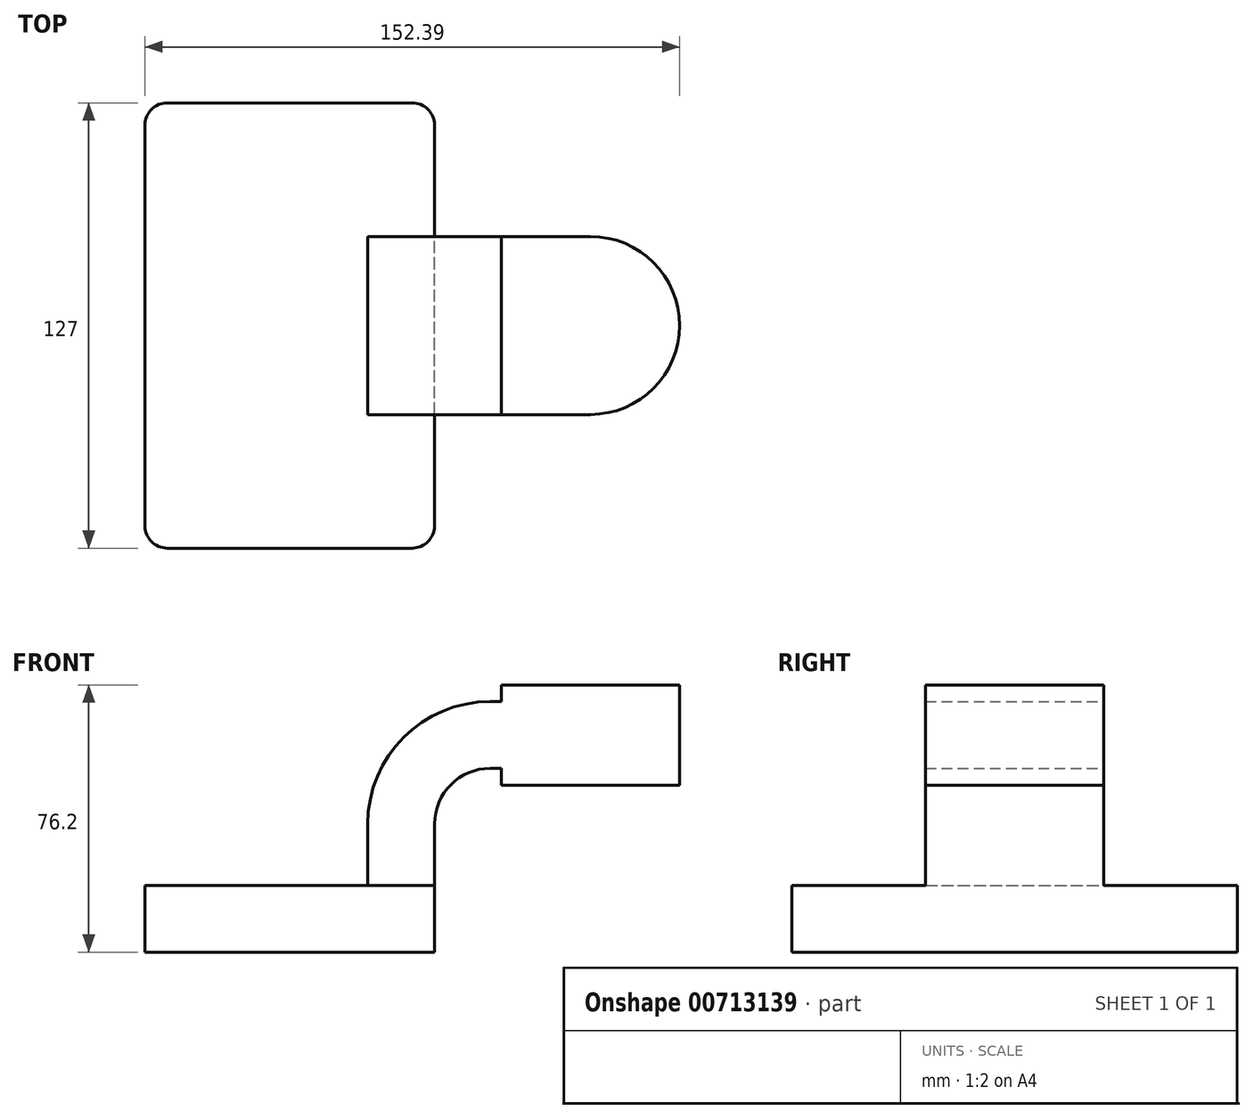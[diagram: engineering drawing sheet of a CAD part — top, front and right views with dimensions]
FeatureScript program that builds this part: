
annotation { "Feature Type Name" : "Feature", "Feature Type Description" : "" }
export const myFeature = defineFeature(function(context is Context, id is Id, definition is map)
    precondition{}
    {
        {
            var Q0;
            Q0=qCreatedBy(makeId("Front.planeOp"),FACE);
            var sketch = newSketch(context, id + "F0", { "sketchPlane" : qUnion([Q0])});
            skLineSegment(sketch, "E0.bottom", {"start": v(-41.28, -9.53) * mm, "end": v(41.28, -9.53) * mm});
            skLineSegment(sketch, "E0.top", {"start": v(-41.28, 9.53) * mm, "end": v(41.28, 9.53) * mm});
            skLineSegment(sketch, "E0.left", {"start": v(-41.28, -9.53) * mm, "end": v(-41.28, 9.53) * mm});
            skLineSegment(sketch, "E0.right", {"start": v(41.28, -9.53) * mm, "end": v(41.28, 9.52) * mm});
            skPoint(sketch, "E0.middle", {"position": v(0, 0) * mm});
            skLineSegment(sketch, "E1", {"start": v(41.28, 9.53) * mm, "end": v(41.28, 27) * mm});
            skArc(sketch, "E2", {"start": v(41.28, 27) * mm, "mid": v(45.92, 38.23) * mm, "end": v(57.15, 42.88) * mm});
            skLineSegment(sketch, "E3.bottom", {"start": v(60.32, 38.1) * mm, "end": v(111.12, 38.1) * mm});
            skLineSegment(sketch, "E3.top", {"start": v(60.32, 66.67) * mm, "end": v(111.12, 66.67) * mm});
            skLineSegment(sketch, "E3.left", {"start": v(60.32, 38.1) * mm, "end": v(60.32, 66.68) * mm});
            skLineSegment(sketch, "E3.right", {"start": v(111.12, 38.1) * mm, "end": v(111.12, 66.68) * mm});
            skPoint(sketch, "E3.middle", {"position": v(85.72, 52.39) * mm});
            skLineSegment(sketch, "E4", {"start": v(57.15, 42.88) * mm, "end": v(81.51, 42.88) * mm});
            skLineSegment(sketch, "E5.0", {"start": v(57.15, 61.93) * mm, "end": v(81.51, 61.93) * mm});
            skArc(sketch, "E5.1", {"start": v(22.23, 27) * mm, "mid": v(32.45, 51.7) * mm, "end": v(57.15, 61.93) * mm});
            skLineSegment(sketch, "E5.2", {"start": v(22.23, 9.53) * mm, "end": v(22.23, 27) * mm});
            skLineSegment(sketch, "E6", {"start": v(85.72, 38.1) * mm, "end": v(85.72, 66.67) * mm});
            skFitSpline(sketch, "E7", {"points": [v(-41.28, 9.53) * mm, v(57.15, 61.93) * mm], "startDerivative": vector(39.13, 93.1) * mm, "endDerivative": vector(146.37, -52.4) * mm});
            skSolve(sketch);
        }
        {
            var Q0;
            Q0=makeQuery(id+"F0.imprint","IMPRINT",FACE,{"disambiguationData":[TD([[makeQuery(id+"F0.imprint","IMPRINT",EDGE,{"derivedFrom":sQuery(id+"F0.wireOp",EDGE,"E0.bottom")}),1.0]])]});
            extrude(context, id + "F1", {"entities" : qUnion([Q0]), "surfaceOperationType" : NewSurfaceOperationType.ADD, "endBound" : BoundingType.SYMMETRIC, "depth" : 127 * mm, "offsetDistance" : 25.4 * mm});
        }
        {
            var Q0;
            {var subQ2=sQuery(id+"F0.wireOp",EDGE,"E1");Q0=makeQuery(id+"F0.imprint","IMPRINT",FACE,{"disambiguationData":[TD([[makeQuery(id+"F0.imprint","IMPRINT",EDGE,{"derivedFrom":subQ2}),1.0]])]});}
            var Q1;
            {var subQ6=sQuery(id+"F0.wireOp",EDGE,"E6");Q1=makeQuery(id+"F0.imprint","IMPRINT",FACE,{"disambiguationData":[TD([[makeQuery(id+"F0.imprint","IMPRINT",EDGE,{"derivedFrom":subQ6}),1.0]])]});}
            extrude(context, id + "F2", {"entities" : qUnion([Q0, Q1]), "operationType" : NewBodyOperationType.ADD, "endBound" : BoundingType.SYMMETRIC, "depth" : 50.8 * mm, "offsetDistance" : 25.4 * mm});
        }
        {
            var Q0;
            Q0=makeQuery(id+"F0.imprint","IMPRINT",FACE,{"disambiguationData":[TD([[makeQuery(id+"F0.imprint","IMPRINT",EDGE,{"derivedFrom":sQuery(id+"F0.wireOp",EDGE,"E5.1")}),1.0]])]});
            extrude(context, id + "F3", {"entities" : qUnion([Q0]), "operationType" : NewBodyOperationType.ADD, "endBound" : BoundingType.SYMMETRIC, "depth" : 15.88 * mm, "offsetDistance" : 25.4 * mm});
        }
        {
            var Q0;
            {var subQ0=sQuery(id+"F0.wireOp",EDGE,"E3.right");Q0=makeQuery(id+"F0.imprint","IMPRINT",FACE,{"disambiguationData":[TD([[makeQuery(id+"F0.imprint","IMPRINT",EDGE,{"derivedFrom":subQ0}),1.0]])]});}
            var Q1;
            Q1=sQuery(id+"F0.wireOp",EDGE,"E6");
            revolve(context, id + "F4", {"operationType" : NewBodyOperationType.ADD, "surfaceOperationType" : NewSurfaceOperationType.NEW, "entities" : qUnion([Q0]), "axis" : qUnion([Q1]), "revolveType" : RevolveType.FULL});
        }
        {
            var Q0;
            Q0=makeQuery(id+"F1.opExtrude","CAP_EDGE",EDGE,{"disambiguationData":[OSD([sQuery(id+"F0.wireOp",EDGE,"E0.left")])],"isStart":false});
            var Q1;
            Q1=makeQuery(id+"F1.opExtrude","CAP_EDGE",EDGE,{"disambiguationData":[OSD([sQuery(id+"F0.wireOp",EDGE,"E0.right")])],"isStart":false});
            var Q2;
            Q2=makeQuery(id+"F1.opExtrude","CAP_EDGE",EDGE,{"disambiguationData":[OSD([sQuery(id+"F0.wireOp",EDGE,"E0.right")])],"isStart":true});
            var Q3;
            Q3=makeQuery(id+"F1.opExtrude","CAP_EDGE",EDGE,{"disambiguationData":[OSD([sQuery(id+"F0.wireOp",EDGE,"E0.left")])],"isStart":true});
            fillet(context, id + "F5", {"entities" : qUnion([Q0, Q1, Q2, Q3]), "radius" : 6.35 * mm, "tangentPropagation" : true, "allowEdgeOverflow" : false});
        }
    });
